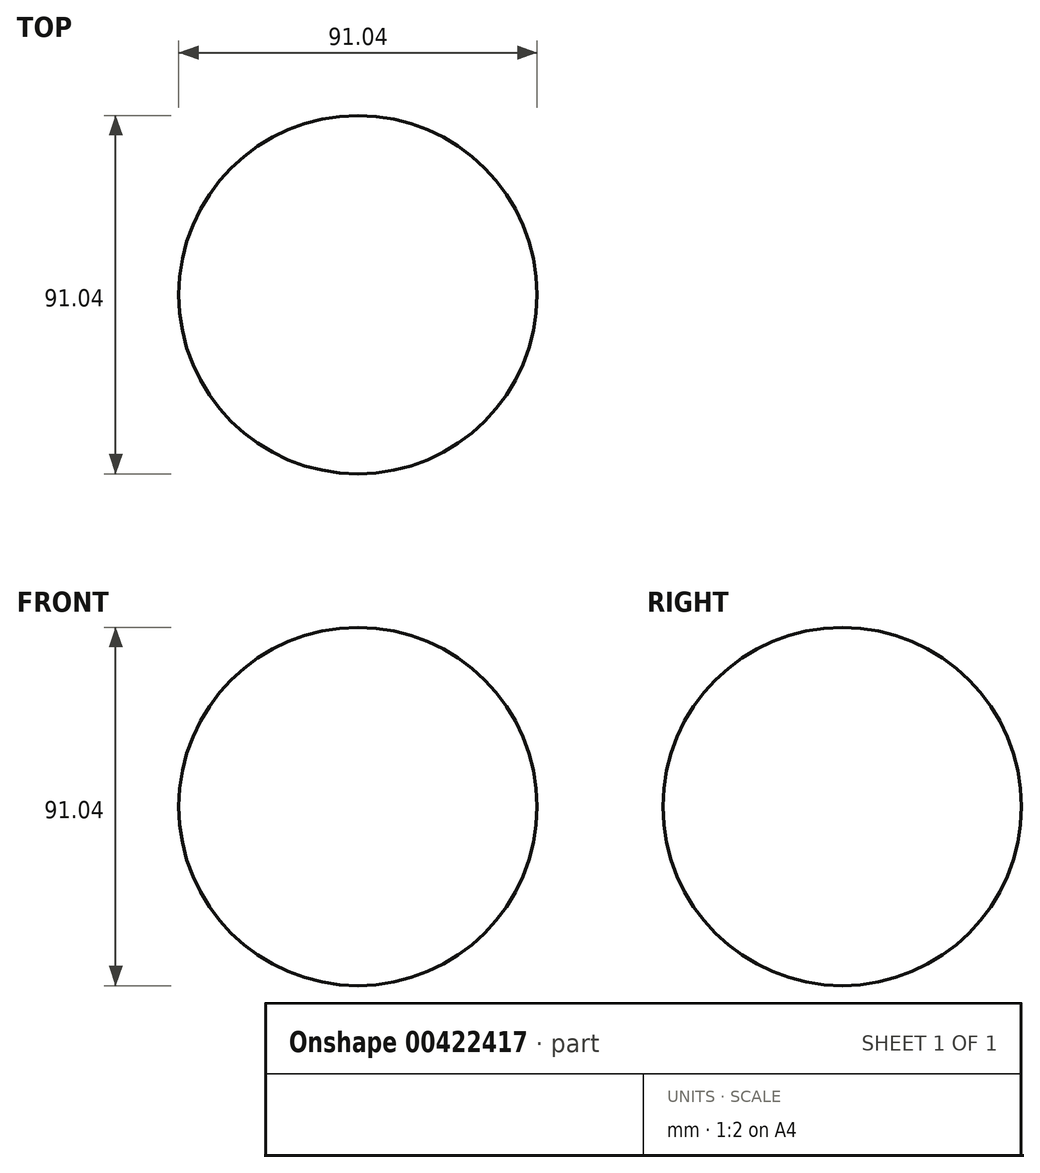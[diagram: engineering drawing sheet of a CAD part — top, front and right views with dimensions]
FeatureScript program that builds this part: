
annotation { "Feature Type Name" : "Feature", "Feature Type Description" : "" }
export const myFeature = defineFeature(function(context is Context, id is Id, definition is map)
    precondition{}
    {
        {
            var Q0;
            Q0=qCreatedBy(makeId("Front.planeOp"),FACE);
            var sketch = newSketch(context, id + "F0", { "sketchPlane" : qUnion([Q0])});
            skPoint(sketch, "E0.end.orphan", {"position": v(0, 35.7) * mm});
            skPoint(sketch, "E0.start.orphan", {"position": v(0, -14.32) * mm});
            skArc(sketch, "E1", {"start": v(0, -45.52) * mm, "mid": v(45.52, 0) * mm, "end": v(0, 45.52) * mm});
            skLineSegment(sketch, "E2", {"start": v(0, 45.52) * mm, "end": v(0, -45.52) * mm});
            skSolve(sketch);
        }
        {
            var Q0;
            Q0=makeQuery(id+"F0.imprint","IMPRINT",FACE,{"disambiguationData":[TD([[makeQuery(id+"F0.imprint","IMPRINT",EDGE,{"derivedFrom":sQuery(id+"F0.wireOp",EDGE,"E1")}),1.0]])]});
            var sketch = newSketch(context, id + "F1", { "sketchPlane" : qUnion([Q0])});
            skSolve(sketch);
        }
        {
            var Q0;
            Q0 = qSketchRegion(id + "F1", true);
            var Q1;
            Q1=makeQuery(id+"F0.imprint","IMPRINT",FACE,{"disambiguationData":[TD([[makeQuery(id+"F0.imprint","IMPRINT",EDGE,{"derivedFrom":sQuery(id+"F0.wireOp",EDGE,"E1")}),1.0]])]});
            var Q2;
            Q2=sQuery(id+"F0.wireOp",EDGE,"E2");
            revolve(context, id + "F2", {"entities" : qUnion([Q0, Q1]), "axis" : qUnion([Q2]), "revolveType" : RevolveType.FULL});
        }
    });
